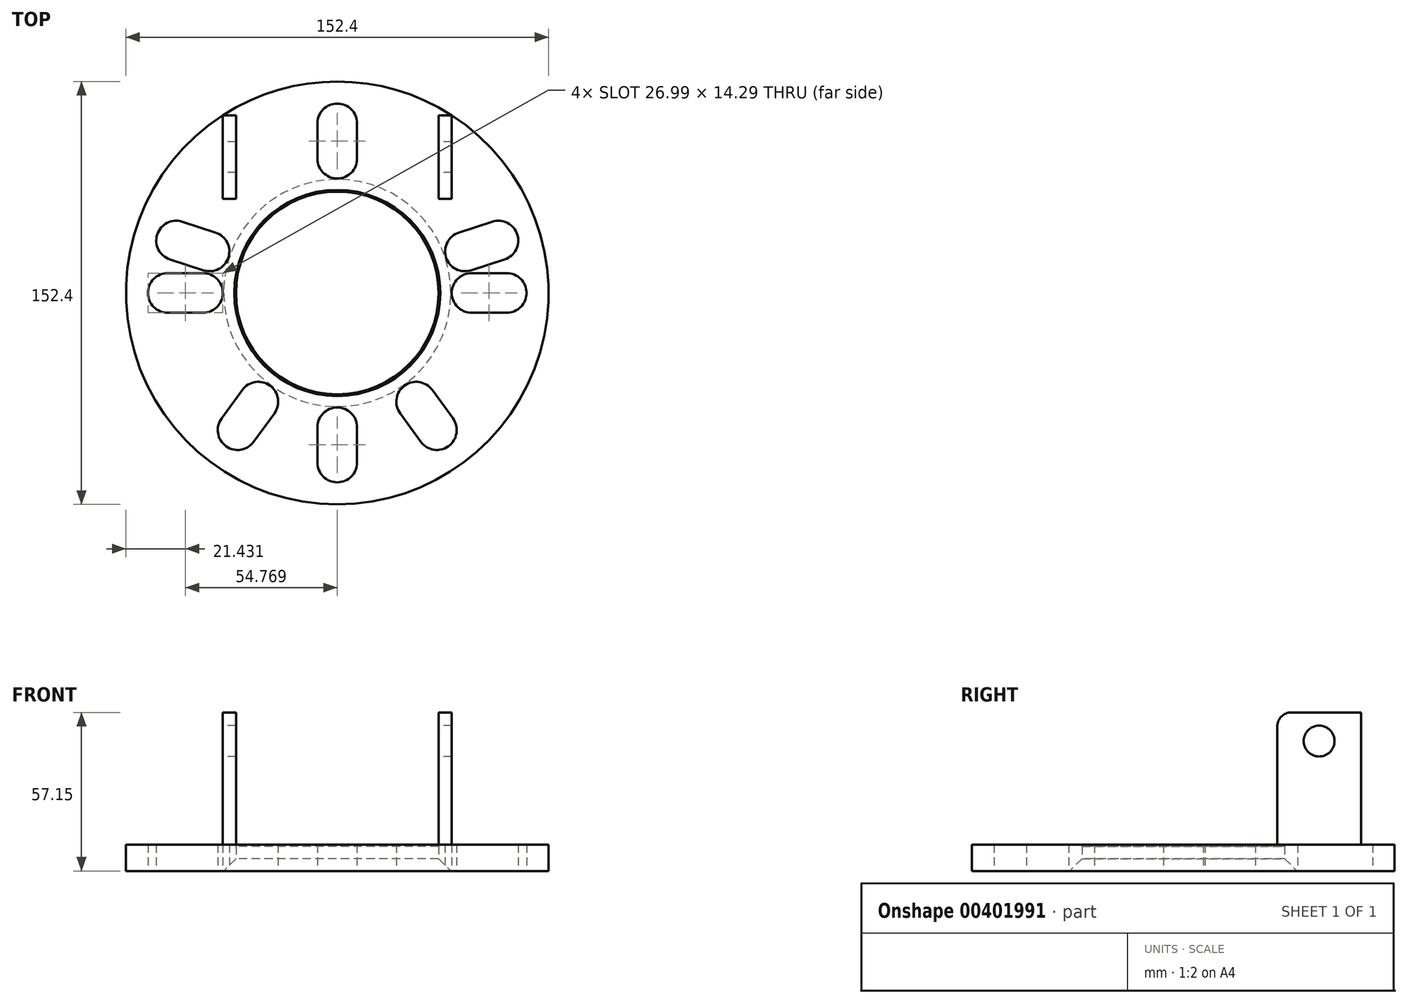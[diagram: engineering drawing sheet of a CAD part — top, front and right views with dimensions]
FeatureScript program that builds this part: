
annotation { "Feature Type Name" : "Feature", "Feature Type Description" : "" }
export const myFeature = defineFeature(function(context is Context, id is Id, definition is map)
    precondition{}
    {
        {
            var Q0;
            Q0=qCreatedBy(makeId("Top.planeOp"),FACE);
            var sketch = newSketch(context, id + "F0", { "sketchPlane" : qUnion([Q0])});
            skCircle(sketch, "E0", {"center": v(0, 0) * mm, "radius": 76.2 * mm});
            skCircle(sketch, "E1", {"center": v(0, 0) * mm, "radius": 36.51 * mm});
            skArc(sketch, "E2", {"start": v(7.14, 61.12) * mm, "mid": v(0, 68.26) * mm, "end": v(-7.14, 61.12) * mm});
            skArc(sketch, "E3", {"start": v(-7.14, 48.42) * mm, "mid": v(0, 41.28) * mm, "end": v(7.14, 48.42) * mm});
            skLineSegment(sketch, "E4", {"start": v(7.14, 61.12) * mm, "end": v(7.14, 48.42) * mm});
            skLineSegment(sketch, "E5", {"start": v(-7.14, 61.12) * mm, "end": v(-7.14, 48.42) * mm});
            skLineSegment(sketch, "E6.1.0", {"start": v(-60.33, 12.1) * mm, "end": v(-48.26, 8.17) * mm});
            skArc(sketch, "E6.1.1", {"start": v(-48.26, 8.17) * mm, "mid": v(-39.25, 12.75) * mm, "end": v(-43.84, 21.76) * mm});
            skLineSegment(sketch, "E6.1.2", {"start": v(-55.92, 25.68) * mm, "end": v(-43.84, 21.76) * mm});
            skArc(sketch, "E6.1.3", {"start": v(-55.92, 25.68) * mm, "mid": v(-64.92, 21.1) * mm, "end": v(-60.33, 12.1) * mm});
            skLineSegment(sketch, "E6.2.0", {"start": v(-30.15, -53.65) * mm, "end": v(-22.68, -43.37) * mm});
            skArc(sketch, "E6.2.1", {"start": v(-22.68, -43.37) * mm, "mid": v(-24.26, -33.4) * mm, "end": v(-34.24, -34.97) * mm});
            skLineSegment(sketch, "E6.2.2", {"start": v(-41.7, -45.25) * mm, "end": v(-34.24, -34.97) * mm});
            skArc(sketch, "E6.2.3", {"start": v(-41.7, -45.25) * mm, "mid": v(-40.12, -55.23) * mm, "end": v(-30.15, -53.65) * mm});
            skLineSegment(sketch, "E7.2.3.0", {"start": v(41.7, -45.25) * mm, "end": v(34.24, -34.97) * mm});
            skArc(sketch, "E7.3.3.0", {"start": v(34.24, -34.97) * mm, "mid": v(24.26, -33.4) * mm, "end": v(22.68, -43.37) * mm});
            skLineSegment(sketch, "E7.7.3.0", {"start": v(30.15, -53.65) * mm, "end": v(22.68, -43.37) * mm});
            skArc(sketch, "E7.10.3.0", {"start": v(30.15, -53.65) * mm, "mid": v(40.12, -55.23) * mm, "end": v(41.7, -45.25) * mm});
            skLineSegment(sketch, "E7.2.4.0", {"start": v(55.92, 25.68) * mm, "end": v(43.84, 21.76) * mm});
            skArc(sketch, "E7.3.4.0", {"start": v(43.84, 21.76) * mm, "mid": v(39.25, 12.75) * mm, "end": v(48.26, 8.17) * mm});
            skLineSegment(sketch, "E7.7.4.0", {"start": v(60.33, 12.1) * mm, "end": v(48.26, 8.17) * mm});
            skArc(sketch, "E7.10.4.0", {"start": v(60.33, 12.1) * mm, "mid": v(64.92, 21.1) * mm, "end": v(55.92, 25.68) * mm});
            skArc(sketch, "E8.1.0", {"start": v(-61.12, 7.14) * mm, "mid": v(-68.26, 0) * mm, "end": v(-61.12, -7.14) * mm});
            skLineSegment(sketch, "E8.1.1", {"start": v(-61.12, -7.14) * mm, "end": v(-48.42, -7.14) * mm});
            skArc(sketch, "E8.1.2", {"start": v(-48.42, -7.14) * mm, "mid": v(-41.28, 0) * mm, "end": v(-48.42, 7.14) * mm});
            skLineSegment(sketch, "E8.1.3", {"start": v(-61.12, 7.14) * mm, "end": v(-48.42, 7.14) * mm});
            skArc(sketch, "E8.2.0", {"start": v(-7.14, -61.12) * mm, "mid": v(0, -68.26) * mm, "end": v(7.14, -61.12) * mm});
            skLineSegment(sketch, "E8.2.1", {"start": v(7.14, -61.12) * mm, "end": v(7.14, -48.42) * mm});
            skArc(sketch, "E8.2.2", {"start": v(7.14, -48.42) * mm, "mid": v(0, -41.28) * mm, "end": v(-7.14, -48.42) * mm});
            skLineSegment(sketch, "E8.2.3", {"start": v(-7.14, -61.12) * mm, "end": v(-7.14, -48.42) * mm});
            skArc(sketch, "E8.3.0", {"start": v(61.12, -7.14) * mm, "mid": v(68.26, 0) * mm, "end": v(61.12, 7.14) * mm});
            skLineSegment(sketch, "E8.3.1", {"start": v(61.12, 7.14) * mm, "end": v(48.42, 7.14) * mm});
            skArc(sketch, "E8.3.2", {"start": v(48.42, 7.14) * mm, "mid": v(41.28, 0) * mm, "end": v(48.42, -7.14) * mm});
            skLineSegment(sketch, "E8.3.3", {"start": v(61.12, -7.14) * mm, "end": v(48.42, -7.14) * mm});
            skSolve(sketch);
        }
        {
            var Q0;
            Q0=makeQuery(id+"F0.imprint","IMPRINT",FACE,{"disambiguationData":[TD([[makeQuery(id+"F0.imprint","IMPRINT",EDGE,{"derivedFrom":sQuery(id+"F0.wireOp",EDGE,"E1")}),-1.0]])]});
            extrude(context, id + "F1", {"entities" : qUnion([Q0]), "depth" : 9.52 * mm});
        }
        {
            var Q0;
            Q0=makeQuery(id+"F1.opExtrude","CAP_FACE",FACE,{"disambiguationData":[OSD([sQuery(id+"F0.wireOp",EDGE,"E1"),sQuery(id+"F0.wireOp",EDGE,"E2"),sQuery(id+"F0.wireOp",EDGE,"E3"),sQuery(id+"F0.wireOp",EDGE,"E4"),sQuery(id+"F0.wireOp",EDGE,"E5"),sQuery(id+"F0.wireOp",EDGE,"E0"),sQuery(id+"F0.wireOp",EDGE,"E6.1.0"),sQuery(id+"F0.wireOp",EDGE,"E6.1.1"),sQuery(id+"F0.wireOp",EDGE,"E6.1.2"),sQuery(id+"F0.wireOp",EDGE,"E6.1.3"),sQuery(id+"F0.wireOp",EDGE,"E6.2.0"),sQuery(id+"F0.wireOp",EDGE,"E6.2.1"),sQuery(id+"F0.wireOp",EDGE,"E6.2.2"),sQuery(id+"F0.wireOp",EDGE,"E6.2.3"),sQuery(id+"F0.wireOp",EDGE,"E7.2.3.0"),sQuery(id+"F0.wireOp",EDGE,"E7.3.3.0"),sQuery(id+"F0.wireOp",EDGE,"E7.7.3.0"),sQuery(id+"F0.wireOp",EDGE,"E7.10.3.0"),sQuery(id+"F0.wireOp",EDGE,"E7.2.4.0"),sQuery(id+"F0.wireOp",EDGE,"E7.3.4.0"),sQuery(id+"F0.wireOp",EDGE,"E7.7.4.0"),sQuery(id+"F0.wireOp",EDGE,"E7.10.4.0"),sQuery(id+"F0.wireOp",EDGE,"E8.1.0"),sQuery(id+"F0.wireOp",EDGE,"E8.1.1"),sQuery(id+"F0.wireOp",EDGE,"E8.1.2"),sQuery(id+"F0.wireOp",EDGE,"E8.1.3"),sQuery(id+"F0.wireOp",EDGE,"E8.2.0"),sQuery(id+"F0.wireOp",EDGE,"E8.2.1"),sQuery(id+"F0.wireOp",EDGE,"E8.2.2"),sQuery(id+"F0.wireOp",EDGE,"E8.2.3"),sQuery(id+"F0.wireOp",EDGE,"E8.3.0"),sQuery(id+"F0.wireOp",EDGE,"E8.3.1"),sQuery(id+"F0.wireOp",EDGE,"E8.3.2"),sQuery(id+"F0.wireOp",EDGE,"E8.3.3")])],"isStart":false});
            var sketch = newSketch(context, id + "F2", { "sketchPlane" : qUnion([Q0])});
            skLineSegment(sketch, "E9", {"start": v(41.28, 64.05) * mm, "end": v(-41.28, 64.05) * mm});
            skLineSegment(sketch, "E10.bottom", {"start": v(41.28, 64.05) * mm, "end": v(36.51, 64.05) * mm});
            skLineSegment(sketch, "E10.top", {"start": v(41.27, 33.9) * mm, "end": v(36.51, 33.9) * mm});
            skLineSegment(sketch, "E10.left", {"start": v(41.28, 64.05) * mm, "end": v(41.28, 33.9) * mm});
            skLineSegment(sketch, "E10.right", {"start": v(36.51, 64.05) * mm, "end": v(36.51, 33.9) * mm});
            skLineSegment(sketch, "E11.bottom", {"start": v(-41.28, 64.05) * mm, "end": v(-36.51, 64.05) * mm});
            skLineSegment(sketch, "E11.top", {"start": v(-41.28, 33.9) * mm, "end": v(-36.51, 33.9) * mm});
            skLineSegment(sketch, "E11.left", {"start": v(-41.28, 64.05) * mm, "end": v(-41.28, 33.9) * mm});
            skLineSegment(sketch, "E11.right", {"start": v(-36.51, 64.05) * mm, "end": v(-36.51, 33.9) * mm});
            skSolve(sketch);
        }
        {
            var Q0;
            Q0 = qSketchRegion(id + "F2", true);
            extrude(context, id + "F3", {"entities" : qUnion([Q0]), "operationType" : NewBodyOperationType.ADD, "depth" : 47.62 * mm});
        }
        {
            var Q0;
            Q0=makeQuery(id+"F1.opExtrude","CAP_EDGE",EDGE,{"disambiguationData":[OSD([sQuery(id+"F0.wireOp",EDGE,"E1")])],"isStart":true});
            chamfer(context, id + "F4", {"entities" : qUnion([Q0]), "width" : 4.44 * mm, "tangentPropagation" : true});
        }
        {
            var Q0;
            Q0=makeQuery(id+"F3.opExtrude","SWEPT_FACE",FACE,{"disambiguationData":[OSD([sQuery(id+"F2.wireOp",EDGE,"E10.left")])]});
            var sketch = newSketch(context, id + "F5", { "sketchPlane" : qUnion([Q0])});
            skPoint(sketch, "E12", {"position": v(48.97, 46.83) * mm});
            skPoint(sketch, "E12.positionSnap0", {"position": v(48.97, 57.15) * mm});
            skSolve(sketch);
        }
        {
            var Q0;
            Q0=sQuery(id+"F5.wireOp",VERTEX,"E12");
            var Q1;
            Q1=makeQuery(id+"F1.opExtrude","SWEPT_BODY",BODY,{"disambiguationData":[OSD([sQuery(id+"F0.wireOp",EDGE,"E1"),sQuery(id+"F0.wireOp",EDGE,"E2"),sQuery(id+"F0.wireOp",EDGE,"E3"),sQuery(id+"F0.wireOp",EDGE,"E4"),sQuery(id+"F0.wireOp",EDGE,"E5"),sQuery(id+"F0.wireOp",EDGE,"E0"),sQuery(id+"F0.wireOp",EDGE,"E6.1.0"),sQuery(id+"F0.wireOp",EDGE,"E6.1.1"),sQuery(id+"F0.wireOp",EDGE,"E6.1.2"),sQuery(id+"F0.wireOp",EDGE,"E6.1.3"),sQuery(id+"F0.wireOp",EDGE,"E6.2.0"),sQuery(id+"F0.wireOp",EDGE,"E6.2.1"),sQuery(id+"F0.wireOp",EDGE,"E6.2.2"),sQuery(id+"F0.wireOp",EDGE,"E6.2.3"),sQuery(id+"F0.wireOp",EDGE,"E7.2.3.0"),sQuery(id+"F0.wireOp",EDGE,"E7.3.3.0"),sQuery(id+"F0.wireOp",EDGE,"E7.7.3.0"),sQuery(id+"F0.wireOp",EDGE,"E7.10.3.0"),sQuery(id+"F0.wireOp",EDGE,"E7.2.4.0"),sQuery(id+"F0.wireOp",EDGE,"E7.3.4.0"),sQuery(id+"F0.wireOp",EDGE,"E7.7.4.0"),sQuery(id+"F0.wireOp",EDGE,"E7.10.4.0"),sQuery(id+"F0.wireOp",EDGE,"E8.1.0"),sQuery(id+"F0.wireOp",EDGE,"E8.1.1"),sQuery(id+"F0.wireOp",EDGE,"E8.1.2"),sQuery(id+"F0.wireOp",EDGE,"E8.1.3"),sQuery(id+"F0.wireOp",EDGE,"E8.2.0"),sQuery(id+"F0.wireOp",EDGE,"E8.2.1"),sQuery(id+"F0.wireOp",EDGE,"E8.2.2"),sQuery(id+"F0.wireOp",EDGE,"E8.2.3"),sQuery(id+"F0.wireOp",EDGE,"E8.3.0"),sQuery(id+"F0.wireOp",EDGE,"E8.3.1"),sQuery(id+"F0.wireOp",EDGE,"E8.3.2"),sQuery(id+"F0.wireOp",EDGE,"E8.3.3")])]});
            hole(context, id + "F6", {"style" : HoleStyle.SIMPLE, "endStyle" : HoleEndStyle.THROUGH, "holeDiameter" : 11.1 * mm, "isTappedThrough" : true, "tappedDepth" : 12.7 * mm, "tapClearance" : 3, "locations" : qUnion([Q0]), "scope" : qUnion([Q1])});
        }
        {
            var Q0;
            Q0=makeQuery(id+"F3.opExtrude","CAP_EDGE",EDGE,{"disambiguationData":[OSD([sQuery(id+"F2.wireOp",EDGE,"E10.top")])],"isStart":false});
            var Q1;
            Q1=makeQuery(id+"F3.opExtrude","CAP_EDGE",EDGE,{"disambiguationData":[OSD([sQuery(id+"F2.wireOp",EDGE,"E10.bottom")])],"isStart":false});
            var Q2;
            Q2=makeQuery(id+"F3.opExtrude","CAP_EDGE",EDGE,{"disambiguationData":[OSD([sQuery(id+"F2.wireOp",EDGE,"E11.top")])],"isStart":false});
            var Q3;
            Q3=makeQuery(id+"F3.opExtrude","CAP_EDGE",EDGE,{"disambiguationData":[OSD([sQuery(id+"F2.wireOp",EDGE,"E11.bottom")])],"isStart":false});
            fillet(context, id + "F7", {"entities" : qUnion([Q0, Q1, Q2, Q3]), "radius" : 5.08 * mm, "tangentPropagation" : true, "allowEdgeOverflow" : false});
        }
        {
            var Q0;
            Q0=makeQuery(id+"F1.opExtrude","CAP_EDGE",EDGE,{"disambiguationData":[OSD([sQuery(id+"F0.wireOp",EDGE,"E1")])],"isStart":false});
            chamfer(context, id + "F8", {"entities" : qUnion([Q0]), "width" : 0.64 * mm, "tangentPropagation" : true});
        }
    });
